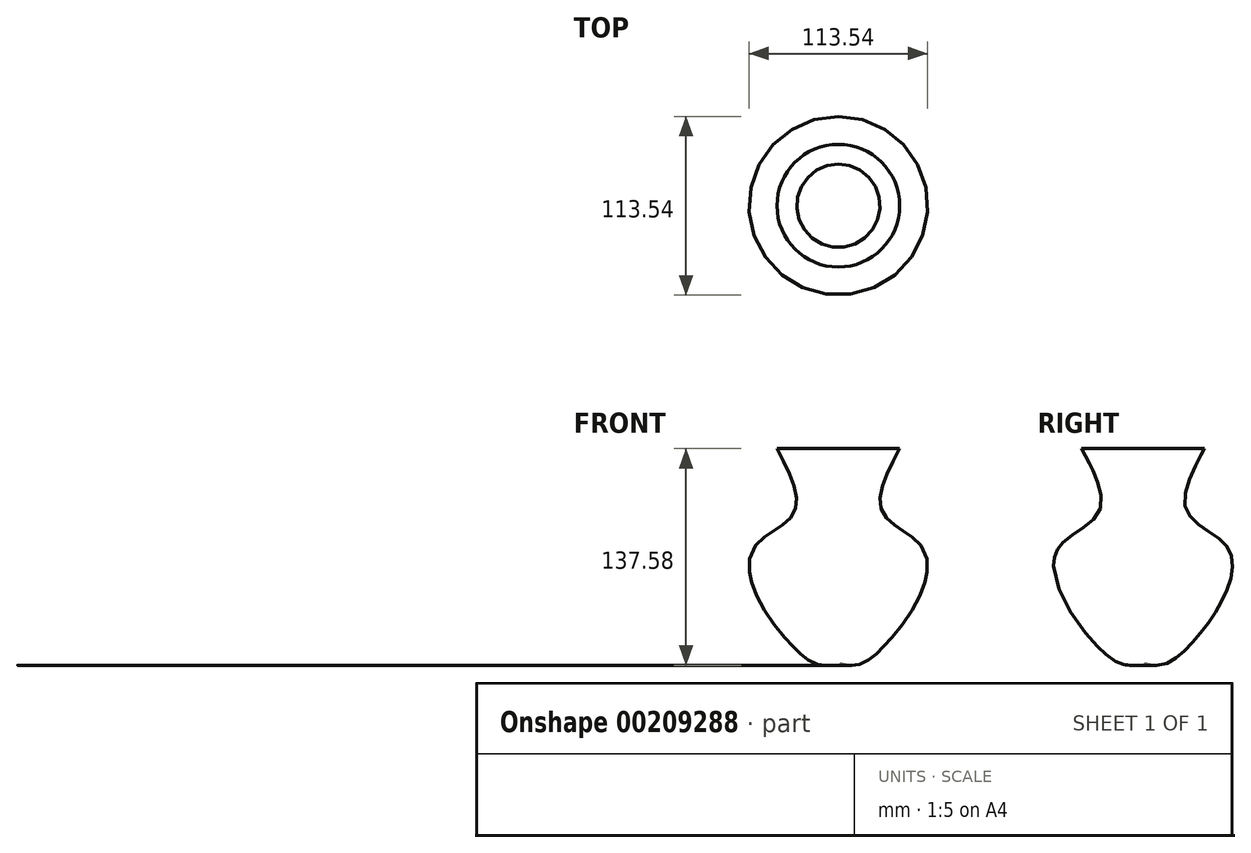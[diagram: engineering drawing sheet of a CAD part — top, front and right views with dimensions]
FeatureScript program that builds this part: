
annotation { "Feature Type Name" : "Feature", "Feature Type Description" : "" }
export const myFeature = defineFeature(function(context is Context, id is Id, definition is map)
    precondition{}
    {
        {
            var Q0;
            Q0=qCreatedBy(makeId("Right.planeOp"),FACE);
            var sketch = newSketch(context, id + "F0", { "sketchPlane" : qUnion([Q0])});
            skFitSpline(sketch, "E0", {"points": [v(38.99, 69.3) * mm, v(26.73, 32.55) * mm, v(53.02, 7.37) * mm, v(51.69, -24.26) * mm, v(27.85, -57.46) * mm, v(0, -66.6) * mm], "startDerivative": vector(-23.52, -59.72) * mm, "endDerivative": vector(-210.38, 78.99) * mm});
            skLineSegment(sketch, "E1", {"start": v(0, 71.11) * mm, "end": v(0, 92.06) * mm});
            skSolve(sketch);
        }
        {
            var Q0;
            Q0=sQuery(id+"F0.wireOp",EDGE,"E0");
            var Q1;
            Q1=sQuery(id+"F0.wireOp",EDGE,"E1");
            revolve(context, id + "F1", {"bodyType" : ToolBodyType.SURFACE, "surfaceEntities" : qUnion([Q0]), "axis" : qUnion([Q1]), "revolveType" : RevolveType.FULL});
        }
    });
